# Revit family: MaviGard Détecteur de Gaz ,Gaz Naturel type du mur - plafond
name_source: partatom
category: Fire Alarm Devices
units: mm (PartAtom-declared; Revit-internal decimal feet)

## family parameters
Cut with Voids When Loaded = No
Host = Face
Maintain Annotation Orientation = Yes
OmniClass Number = 23.85.30.21
OmniClass Title = Environmental Detection/Registration
Part Type = Normal
Room Calculation Point = No
Round Connector Dimension = Use Diameter
Shared = No

## types (1)
- MaviGard détecteur de gaz Gaz Naturel  type du mur ou plafond
    Adresse ligne 1 = Şerifali Mahallesi Kutup Sokak No:27/1-2-4 Ümraniye TR-34775 İSTANBUL
    Alimentation d'externe = 24 V/DC
    Code de  Performance = EN 50194-1
    Code de Produit = TGDR-1224M
    Cost = 0 $
    Couleur = Blanc
    Default Elevation = 0 mm  [stored 0 ft]
    Description = Détecteur de Gaz Conventionnel
    Deuxime Matèriel = Plastique
    Durée de la garantie Travail = 2
    Durée de la garantie réservé = 2
    Hauteur de Montage = 15-25 cm bas du plafond
    Manuel d'installation = https://mavilielektronik.com
    Manufacturer = Mavili Elektronik Ticaret A.Ş.
    Matériel Principe = Plastique Blanc PC/ABS
    Model = MaviGard
    Numèro de Fax = (+)90 216 466 45 10
    Socles Compatible = MG-3500
    Surface de Montage = Montage au mur ou montage au plafond
    Tempèrature de Fonctionnement = (-10°C) - (+50°C)
    URL = https://www.mavili.com.tr
    Unité de durée de garantie = Ans
    Voltage de fonctionnement (default) = 24 V/DC
    protection de Classe = IP42
    voltage fonction d'opération = 18-33V/DC

note: [stored X ft] marks values corroborated as IEEE doubles in the binary element streams (Revit-internal decimal feet)

## geometry (parser evidence)
native form markers: Sweep x3
no freeform markers — native parametric forms only
